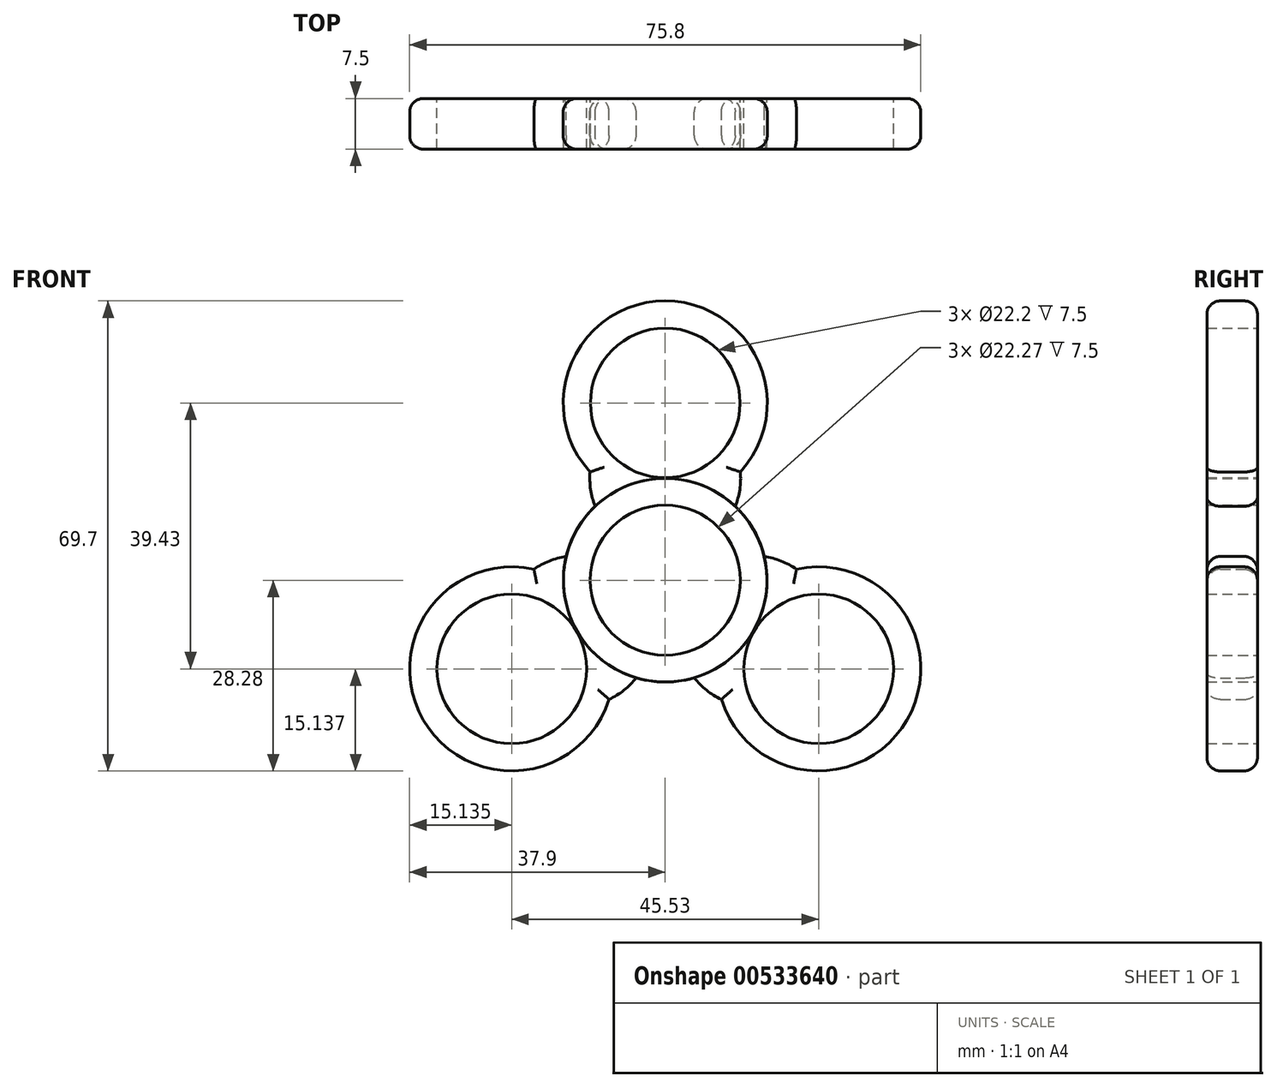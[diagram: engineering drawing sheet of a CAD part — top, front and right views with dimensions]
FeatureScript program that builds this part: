
annotation { "Feature Type Name" : "Feature", "Feature Type Description" : "" }
export const myFeature = defineFeature(function(context is Context, id is Id, definition is map)
    precondition{}
    {
        {
            var Q0;
            Q0=qCreatedBy(makeId("Front.planeOp"),FACE);
            var sketch = newSketch(context, id + "F0", { "sketchPlane" : qUnion([Q0])});
            skCircle(sketch, "E0", {"center": v(0, 0) * mm, "radius": 11.13 * mm});
            skCircle(sketch, "E1", {"center": v(0, 0) * mm, "radius": 15.1 * mm});
            skLineSegment(sketch, "E2", {"start": v(-14.74, 3.27) * mm, "end": v(14.74, 3.27) * mm});
            skArc(sketch, "E3", {"start": v(-9.64, 20.78) * mm, "mid": v(-11.15, 15.96) * mm, "end": v(-10.4, 10.96) * mm});
            skCircle(sketch, "E4", {"center": v(0, 26.29) * mm, "radius": 11.1 * mm});
            skArc(sketch, "E5.trimOffspring", {"start": v(10.4, 10.96) * mm, "mid": v(11.15, 15.96) * mm, "end": v(9.64, 20.78) * mm});
            skCircle(sketch, "E6", {"center": v(0, 26.29) * mm, "radius": 15.13 * mm});
            skSolve(sketch);
        }
        {
            var Q0;
            {var subQ0=sQuery(id+"F0.wireOp",EDGE,"E4");var subQ1=sQuery(id+"F0.wireOp",EDGE,"E3");var subQ2=makeQuery(id+"F0.imprint","INTERSECT",VERTEX,{"derivedFrom":[subQ1,subQ0]});Q0=makeQuery(id+"F0.imprint","IMPRINT",FACE,{"disambiguationData":[TD([[makeQuery(id+"F0.imprint","IMPRINT",EDGE,{"disambiguationData":[TD([[subQ2,-1.0]])],"derivedFrom":subQ1}),-1.0]])]});}
            var Q1;
            {var subQ4=sQuery(id+"F0.wireOp",EDGE,"E2");var subQ8=sQuery(id+"F0.wireOp",EDGE,"E0");var subQ9=makeQuery(id+"F0.imprint","INTERSECT",VERTEX,{"disambiguationData":[OD(0.0)],"derivedFrom":[subQ8,subQ4]});Q1=makeQuery(id+"F0.imprint","IMPRINT",FACE,{"disambiguationData":[TD([[makeQuery(id+"F0.imprint","IMPRINT",EDGE,{"disambiguationData":[TD([[subQ9,1.0]])],"derivedFrom":subQ8}),-1.0]])]});}
            var Q2;
            {var subQ0=sQuery(id+"F0.wireOp",EDGE,"E2");var subQ1=sQuery(id+"F0.wireOp",EDGE,"E0");var subQ2=makeQuery(id+"F0.imprint","INTERSECT",VERTEX,{"disambiguationData":[OD(0.0)],"derivedFrom":[subQ1,subQ0]});Q2=makeQuery(id+"F0.imprint","IMPRINT",FACE,{"disambiguationData":[TD([[makeQuery(id+"F0.imprint","IMPRINT",EDGE,{"disambiguationData":[TD([[subQ2,-1.0]])],"derivedFrom":subQ1}),-1.0]])]});}
            var Q3;
            {var subQ0=sQuery(id+"F0.wireOp",EDGE,"E6");var subQ1=sQuery(id+"F0.wireOp",EDGE,"E1");var subQ2=makeQuery(id+"F0.imprint","INTERSECT",VERTEX,{"disambiguationData":[OD(0.0)],"derivedFrom":[subQ1,subQ0]});Q3=makeQuery(id+"F0.imprint","IMPRINT",FACE,{"disambiguationData":[TD([[makeQuery(id+"F0.imprint","IMPRINT",EDGE,{"disambiguationData":[TD([[subQ2,-1.0]])],"derivedFrom":subQ1}),1.0]])]});}
            var Q4;
            {var subQ5=sQuery(id+"F0.wireOp",EDGE,"E6");var subQ8=sQuery(id+"F0.wireOp",EDGE,"E1");var subQ9=makeQuery(id+"F0.imprint","INTERSECT",VERTEX,{"disambiguationData":[OD(0.0)],"derivedFrom":[subQ8,subQ5]});Q4=makeQuery(id+"F0.imprint","IMPRINT",FACE,{"disambiguationData":[TD([[makeQuery(id+"F0.imprint","IMPRINT",EDGE,{"disambiguationData":[TD([[subQ9,-1.0]])],"derivedFrom":subQ8}),-1.0]])]});}
            var Q5;
            {var subQ0=sQuery(id+"F0.wireOp",EDGE,"E5.trimOffspring");var subQ1=sQuery(id+"F0.wireOp",EDGE,"E1");var subQ2=makeQuery(id+"F0.imprint","INTERSECT",VERTEX,{"derivedFrom":[subQ1,subQ0]});Q5=makeQuery(id+"F0.imprint","IMPRINT",FACE,{"disambiguationData":[TD([[makeQuery(id+"F0.imprint","IMPRINT",EDGE,{"disambiguationData":[TD([[subQ2,-1.0]])],"derivedFrom":subQ1}),-1.0]])]});}
            var Q6;
            {var subQ0=sQuery(id+"F0.wireOp",EDGE,"E3");var subQ1=sQuery(id+"F0.wireOp",EDGE,"E1");var subQ2=makeQuery(id+"F0.imprint","INTERSECT",VERTEX,{"derivedFrom":[subQ1,subQ0]});Q6=makeQuery(id+"F0.imprint","IMPRINT",FACE,{"disambiguationData":[TD([[makeQuery(id+"F0.imprint","IMPRINT",EDGE,{"disambiguationData":[TD([[subQ2,1.0]])],"derivedFrom":subQ1}),-1.0]])]});}
            extrude(context, id + "F1", {"entities" : qUnion([Q0, Q1, Q2, Q3, Q4, Q5, Q6]), "depth" : 7.5 * mm, "offsetDistance" : 25 * mm});
        }
        {
            var Q0;
            Q0=makeQuery(id+"F1.opExtrude","SWEPT_BODY",BODY,{"disambiguationData":[OSD([sQuery(id+"F0.wireOp",EDGE,"E0"),sQuery(id+"F0.wireOp",EDGE,"E1"),sQuery(id+"F0.wireOp",EDGE,"E3"),sQuery(id+"F0.wireOp",EDGE,"E4"),sQuery(id+"F0.wireOp",EDGE,"E5.trimOffspring"),sQuery(id+"F0.wireOp",EDGE,"E6")])]});
            var Q1;
            Q1=makeQuery(id+"F1.opExtrude","CAP_EDGE",EDGE,{"disambiguationData":[OSD([sQuery(id+"F0.wireOp",EDGE,"E0")])],"isStart":false});
            transform(context, id + "F2", {"entities" : qUnion([Q0]), "transformType" : TransformType.ROTATION, "transformAxis" : qUnion([Q1]), "angle" : 120 * degree, "makeCopy" : true});
        }
        {
            var Q0;
            Q0=makeQuery(id+"F2.opPattern","COPY",BODY,{"derivedFrom":makeQuery(id+"F1.opExtrude","SWEPT_BODY",BODY,{"disambiguationData":[OSD([sQuery(id+"F0.wireOp",EDGE,"E0"),sQuery(id+"F0.wireOp",EDGE,"E1"),sQuery(id+"F0.wireOp",EDGE,"E3"),sQuery(id+"F0.wireOp",EDGE,"E4"),sQuery(id+"F0.wireOp",EDGE,"E5.trimOffspring"),sQuery(id+"F0.wireOp",EDGE,"E6")])]}),"instanceName":"1"});
            var Q1;
            Q1=makeQuery(id+"F1.opExtrude","CAP_EDGE",EDGE,{"disambiguationData":[OSD([sQuery(id+"F0.wireOp",EDGE,"E0")])],"isStart":false});
            transform(context, id + "F3", {"entities" : qUnion([Q0]), "transformType" : TransformType.ROTATION, "transformAxis" : qUnion([Q1]), "angle" : 120 * degree, "makeCopy" : true});
        }
        {
            var Q0;
            Q0=makeQuery(id+"F1.opExtrude","CAP_EDGE",EDGE,{"disambiguationData":[OSD([sQuery(id+"F0.wireOp",EDGE,"E6")])],"isStart":false});
            var Q1;
            Q1=makeQuery(id+"F1.opExtrude","CAP_EDGE",EDGE,{"disambiguationData":[OSD([sQuery(id+"F0.wireOp",EDGE,"E3")])],"isStart":false});
            var Q2;
            Q2=makeQuery(id+"F2.opPattern","COPY",EDGE,{"derivedFrom":makeQuery(id+"F1.opExtrude","CAP_EDGE",EDGE,{"disambiguationData":[OSD([sQuery(id+"F0.wireOp",EDGE,"E5.trimOffspring")])],"isStart":false}),"instanceName":"1"});
            var Q3;
            Q3=makeQuery(id+"F2.opPattern","COPY",EDGE,{"derivedFrom":makeQuery(id+"F1.opExtrude","CAP_EDGE",EDGE,{"disambiguationData":[OSD([sQuery(id+"F0.wireOp",EDGE,"E6")])],"isStart":false}),"instanceName":"1"});
            var Q4;
            Q4=makeQuery(id+"F2.opPattern","COPY",EDGE,{"derivedFrom":makeQuery(id+"F1.opExtrude","CAP_EDGE",EDGE,{"disambiguationData":[OSD([sQuery(id+"F0.wireOp",EDGE,"E3")])],"isStart":false}),"instanceName":"1"});
            var Q5;
            Q5=makeQuery(id+"F3.opPattern","COPY",EDGE,{"derivedFrom":makeQuery(id+"F2.opPattern","COPY",EDGE,{"derivedFrom":makeQuery(id+"F1.opExtrude","CAP_EDGE",EDGE,{"disambiguationData":[OSD([sQuery(id+"F0.wireOp",EDGE,"E5.trimOffspring")])],"isStart":false}),"instanceName":"1"}),"instanceName":"1"});
            var Q6;
            Q6=makeQuery(id+"F3.opPattern","COPY",EDGE,{"derivedFrom":makeQuery(id+"F2.opPattern","COPY",EDGE,{"derivedFrom":makeQuery(id+"F1.opExtrude","CAP_EDGE",EDGE,{"disambiguationData":[OSD([sQuery(id+"F0.wireOp",EDGE,"E6")])],"isStart":false}),"instanceName":"1"}),"instanceName":"1"});
            var Q7;
            Q7=makeQuery(id+"F3.opPattern","COPY",EDGE,{"derivedFrom":makeQuery(id+"F2.opPattern","COPY",EDGE,{"derivedFrom":makeQuery(id+"F1.opExtrude","CAP_EDGE",EDGE,{"disambiguationData":[OSD([sQuery(id+"F0.wireOp",EDGE,"E3")])],"isStart":false}),"instanceName":"1"}),"instanceName":"1"});
            var Q8;
            Q8=makeQuery(id+"F1.opExtrude","CAP_EDGE",EDGE,{"disambiguationData":[OSD([sQuery(id+"F0.wireOp",EDGE,"E5.trimOffspring")])],"isStart":false});
            fillet(context, id + "F4", {"entities" : qUnion([Q0, Q1, Q2, Q3, Q4, Q5, Q6, Q7, Q8]), "radius" : 2 * mm, "tangentPropagation" : true, "allowEdgeOverflow" : false});
        }
        {
            var Q0;
            Q0=makeQuery(id+"F1.opExtrude","CAP_EDGE",EDGE,{"disambiguationData":[OSD([sQuery(id+"F0.wireOp",EDGE,"E6")])],"isStart":true});
            var Q1;
            Q1=makeQuery(id+"F1.opExtrude","CAP_EDGE",EDGE,{"disambiguationData":[OSD([sQuery(id+"F0.wireOp",EDGE,"E5.trimOffspring")])],"isStart":true});
            var Q2;
            Q2=makeQuery(id+"F3.opPattern","COPY",EDGE,{"derivedFrom":makeQuery(id+"F2.opPattern","COPY",EDGE,{"derivedFrom":makeQuery(id+"F1.opExtrude","CAP_EDGE",EDGE,{"disambiguationData":[OSD([sQuery(id+"F0.wireOp",EDGE,"E3")])],"isStart":true}),"instanceName":"1"}),"instanceName":"1"});
            var Q3;
            Q3=makeQuery(id+"F3.opPattern","COPY",EDGE,{"derivedFrom":makeQuery(id+"F2.opPattern","COPY",EDGE,{"derivedFrom":makeQuery(id+"F1.opExtrude","CAP_EDGE",EDGE,{"disambiguationData":[OSD([sQuery(id+"F0.wireOp",EDGE,"E5.trimOffspring")])],"isStart":true}),"instanceName":"1"}),"instanceName":"1"});
            var Q4;
            Q4=makeQuery(id+"F3.opPattern","COPY",EDGE,{"derivedFrom":makeQuery(id+"F2.opPattern","COPY",EDGE,{"derivedFrom":makeQuery(id+"F1.opExtrude","CAP_EDGE",EDGE,{"disambiguationData":[OSD([sQuery(id+"F0.wireOp",EDGE,"E6")])],"isStart":true}),"instanceName":"1"}),"instanceName":"1"});
            var Q5;
            Q5=makeQuery(id+"F2.opPattern","COPY",EDGE,{"derivedFrom":makeQuery(id+"F1.opExtrude","CAP_EDGE",EDGE,{"disambiguationData":[OSD([sQuery(id+"F0.wireOp",EDGE,"E3")])],"isStart":true}),"instanceName":"1"});
            var Q6;
            Q6=makeQuery(id+"F2.opPattern","COPY",EDGE,{"derivedFrom":makeQuery(id+"F1.opExtrude","CAP_EDGE",EDGE,{"disambiguationData":[OSD([sQuery(id+"F0.wireOp",EDGE,"E6")])],"isStart":true}),"instanceName":"1"});
            var Q7;
            Q7=makeQuery(id+"F2.opPattern","COPY",EDGE,{"derivedFrom":makeQuery(id+"F1.opExtrude","CAP_EDGE",EDGE,{"disambiguationData":[OSD([sQuery(id+"F0.wireOp",EDGE,"E5.trimOffspring")])],"isStart":true}),"instanceName":"1"});
            var Q8;
            Q8=makeQuery(id+"F1.opExtrude","CAP_EDGE",EDGE,{"disambiguationData":[OSD([sQuery(id+"F0.wireOp",EDGE,"E3")])],"isStart":true});
            fillet(context, id + "F5", {"entities" : qUnion([Q0, Q1, Q2, Q3, Q4, Q5, Q6, Q7, Q8]), "radius" : 2 * mm, "tangentPropagation" : true, "allowEdgeOverflow" : false});
        }
    });
